# Revit family: Node-1 100-800
name_source: partatom
category: Оборудование
revit_build: Autodesk Revit 2016 (Build: 20160126_1600(x64)
units: mm (PartAtom-declared; Revit-internal decimal feet)

## family parameters
Всегда вертикально = Да
На основе рабочей плоскости = Нет
Общий = Нет
При загрузке вырезать с полостями = Нет
Размер круглого соединителя = Использовать диаметр
Тип детали = Нормальный
Точка расчета площади = Нет

## types (8) — shared parameters
Вылет блока = 137 мм
Высота = 312 мм
Высота блока = 200 мм
Ширина = 665 мм
Ширина блока = 267 мм

## per-type parameters (varying)
| type | Внешний радиус подключения | Внутренний радиус подключения | Диаметр внешнего подключения | Длина | Длина подключений | Материал | Расход |
| Node-1 400 | 82 мм | 80 мм | 160 мм | 900 мм | 1000 мм | 100-400 | 166.7 л/с |
| Node-1 300 | 82 мм | 80 мм | 160 мм | 900 мм | 1000 мм | 100-400 | 125.0 л/с |
| Node-1 200 | 82 мм | 80 мм | 160 мм | 900 мм | 1000 мм | 100-400 | 83.3 л/с |
| Node-1 100 | 82 мм | 80 мм | 160 мм | 900 мм | 1000 мм | 100-400 | 41.6 л/с |
| Node-1 500 | 102 мм | 100 мм | 200 мм | 1180 мм | 1280 мм | 500-800 | 173.6 л/с |
| Node-1 600 | 102 мм | 100 мм | 200 мм | 1180 мм | 1280 мм | 500-800 | 191.7 л/с |
| Node-1 700 | 102 мм | 100 мм | 200 мм | 1180 мм | 1280 мм | 500-800 | 225.0 л/с |
| Node-1 800 | 102 мм | 100 мм | 200 мм | 1180 мм | 1280 мм | 500-800 | 257.0 л/с |
